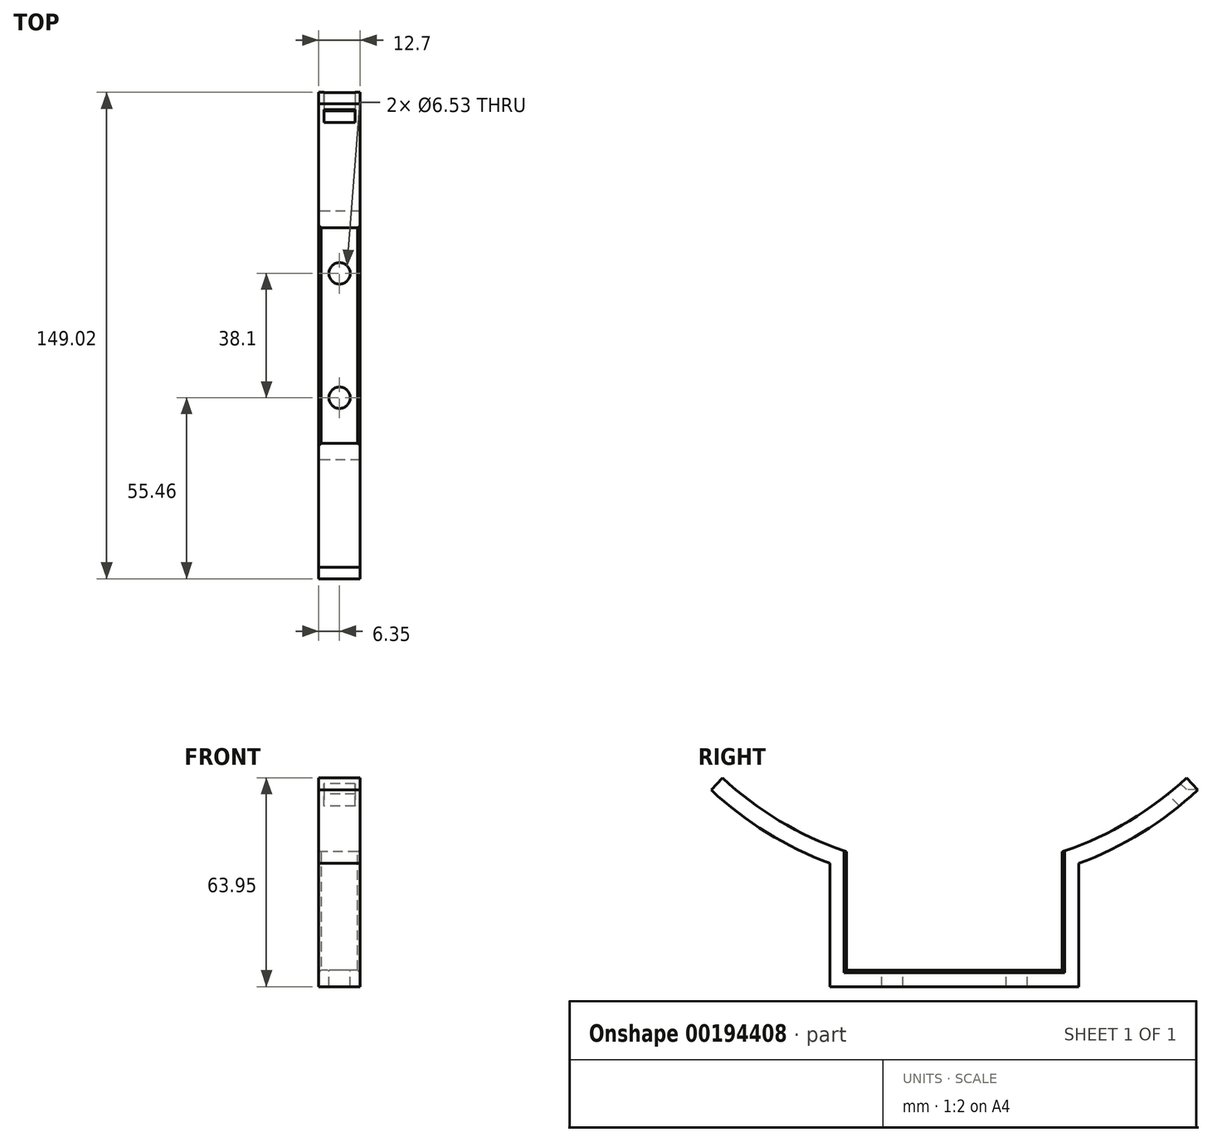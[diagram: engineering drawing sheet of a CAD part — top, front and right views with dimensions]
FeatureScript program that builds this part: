
annotation { "Feature Type Name" : "Feature", "Feature Type Description" : "" }
export const myFeature = defineFeature(function(context is Context, id is Id, definition is map)
    precondition{}
    {
        {
            var Q0;
            Q0=qCreatedBy(makeId("Right.planeOp"),FACE);
            var sketch = newSketch(context, id + "F0", { "sketchPlane" : qUnion([Q0])});
            skLineSegment(sketch, "E0", {"start": v(0, 0) * mm, "end": v(-38.1, 0) * mm});
            skLineSegment(sketch, "E1", {"start": v(-38.1, 0) * mm, "end": v(-38.1, 37.74) * mm});
            skLineSegment(sketch, "E2", {"start": v(0, 5.08) * mm, "end": v(0, 38.1) * mm});
            skLineSegment(sketch, "E3", {"start": v(0, 38.1) * mm, "end": v(0, 135.02) * mm});
            skLineSegment(sketch, "E4", {"start": v(0, 135.02) * mm, "end": v(0, 239.16) * mm});
            skLineSegment(sketch, "E5", {"start": v(0, 135.02) * mm, "end": v(0, 140.1) * mm});
            skArc(sketch, "E6", {"start": v(-71.04, 63.95) * mm, "mid": v(-53.25, 50.6) * mm, "end": v(-33.02, 41.33) * mm});
            skLineSegment(sketch, "E7.0", {"start": v(-33.02, 5.08) * mm, "end": v(-33.02, 38.1) * mm});
            skLineSegment(sketch, "E7.1", {"start": v(0, 5.08) * mm, "end": v(-33.02, 5.08) * mm});
            skArc(sketch, "E8.0", {"start": v(-74.5, 60.24) * mm, "mid": v(-57.42, 47.19) * mm, "end": v(-38.1, 37.74) * mm});
            skLineSegment(sketch, "E9", {"start": v(-71.04, 63.95) * mm, "end": v(-74.5, 60.24) * mm});
            skLineSegment(sketch, "E10", {"start": v(-33.02, 38.1) * mm, "end": v(-33.02, 41.33) * mm});
            skLineSegment(sketch, "E11.MirrorCS", {"start": v(33.02, 38.1) * mm, "end": v(33.02, 41.33) * mm});
            skLineSegment(sketch, "E12.MirrorCS", {"start": v(0, 0) * mm, "end": v(38.1, 0) * mm});
            skLineSegment(sketch, "E13.MirrorCS", {"start": v(33.02, 5.08) * mm, "end": v(33.02, 38.1) * mm});
            skArc(sketch, "E14.MirrorCS", {"start": v(71.04, 63.95) * mm, "mid": v(53.25, 50.6) * mm, "end": v(33.02, 41.33) * mm});
            skLineSegment(sketch, "E15.MirrorCS", {"start": v(0, 5.08) * mm, "end": v(33.02, 5.08) * mm});
            skLineSegment(sketch, "E16.MirrorCS", {"start": v(38.1, 0) * mm, "end": v(38.1, 37.74) * mm});
            skArc(sketch, "E17.MirrorCS", {"start": v(74.5, 60.24) * mm, "mid": v(57.42, 47.19) * mm, "end": v(38.1, 37.74) * mm});
            skLineSegment(sketch, "E18.MirrorCS", {"start": v(71.04, 63.95) * mm, "end": v(74.5, 60.24) * mm});
            skSolve(sketch);
        }
        {
            var Q0;
            Q0=makeQuery(id+"F0.imprint","IMPRINT",FACE,{"disambiguationData":[TD([[makeQuery(id+"F0.imprint","IMPRINT",EDGE,{"derivedFrom":sQuery(id+"F0.wireOp",EDGE,"E0")}),-1.0]])]});
            extrude(context, id + "F1", {"entities" : qUnion([Q0]), "depth" : 12.7 * mm});
        }
        {
            var Q0;
            Q0=makeQuery(id+"F1.opExtrude","SWEPT_FACE",FACE,{"disambiguationData":[OSD([sQuery(id+"F0.wireOp",EDGE,"E7.1"),sQuery(id+"F0.wireOp",EDGE,"E15.MirrorCS")])]});
            var sketch = newSketch(context, id + "F2", { "sketchPlane" : qUnion([Q0])});
            skLineSegment(sketch, "E19", {"start": v(0, 0) * mm, "end": v(6.35, 0) * mm});
            skLineSegment(sketch, "E20", {"start": v(6.35, 0) * mm, "end": v(6.35, 19.05) * mm});
            skLineSegment(sketch, "E21.MirrorCS", {"start": v(6.35, 0) * mm, "end": v(6.35, -19.05) * mm});
            skSolve(sketch);
        }
        {
            var Q0;
            Q0=sQuery(id+"F2.wireOp",VERTEX,"E20.end");
            var Q1;
            Q1=sQuery(id+"F2.wireOp",VERTEX,"E21.MirrorCS.end");
            var Q2;
            Q2=makeQuery(id+"F1.opExtrude","SWEPT_BODY",BODY,{"disambiguationData":[OSD([sQuery(id+"F0.wireOp",EDGE,"E0"),sQuery(id+"F0.wireOp",EDGE,"E1"),sQuery(id+"F0.wireOp",EDGE,"E6"),sQuery(id+"F0.wireOp",EDGE,"E7.0"),sQuery(id+"F0.wireOp",EDGE,"E7.1"),sQuery(id+"F0.wireOp",EDGE,"E8.0"),sQuery(id+"F0.wireOp",EDGE,"E9"),sQuery(id+"F0.wireOp",EDGE,"E10"),sQuery(id+"F0.wireOp",EDGE,"E11.MirrorCS"),sQuery(id+"F0.wireOp",EDGE,"E12.MirrorCS"),sQuery(id+"F0.wireOp",EDGE,"E13.MirrorCS"),sQuery(id+"F0.wireOp",EDGE,"E14.MirrorCS"),sQuery(id+"F0.wireOp",EDGE,"E15.MirrorCS"),sQuery(id+"F0.wireOp",EDGE,"E16.MirrorCS"),sQuery(id+"F0.wireOp",EDGE,"E17.MirrorCS"),sQuery(id+"F0.wireOp",EDGE,"E18.MirrorCS")])]});
            hole(context, id + "F3", {"style" : HoleStyle.SIMPLE, "endStyle" : HoleEndStyle.BLIND, "standardTappedOrClearance" : lookupTablePath({ "standard" : "ANSI", "fit" : "Close", "size" : "1/4", "type" : "Clearance" }), "standardBlindInLast" : lookupTablePath({ "fit" : "Close", "standard" : "ANSI", "size" : "1/4", "type" : "Clearance" }), "holeDiameter" : 6.53 * mm, "holeDepth" : 25.4 * mm, "locations" : qUnion([Q0, Q1]), "scope" : qUnion([Q2])});
        }
        {
            var Q0;
            Q0=makeQuery(id+"F1.opExtrude","SWEPT_EDGE",EDGE,{"disambiguationData":[OSD([sQuery(id+"F0.wireOp",EDGE,"E14.MirrorCS"),sQuery(id+"F0.wireOp",EDGE,"E18.MirrorCS")])]});
            cPlane(context, id + "F4", {"entities" : qUnion([Q0]), "cplaneType" : CPlaneType.LINE_ANGLE, "offset" : 25.4 * mm, "angle" : 45 * degree, "width" : 152.4 * mm, "height" : 152.4 * mm});
        }
        {
            var Q0;
            Q0=makeQuery(id+"F1.opExtrude","SWEPT_EDGE",EDGE,{"disambiguationData":[OSD([sQuery(id+"F0.wireOp",EDGE,"E6"),sQuery(id+"F0.wireOp",EDGE,"E9")])]});
            cPlane(context, id + "F5", {"entities" : qUnion([Q0]), "cplaneType" : CPlaneType.LINE_ANGLE, "offset" : 25.4 * mm, "angle" : 135 * degree, "width" : 152.4 * mm, "height" : 152.4 * mm});
        }
        {
            var Q0;
            Q0=qCreatedBy(id+"F5.planeOp",FACE);
            var sketch = newSketch(context, id + "F6", { "sketchPlane" : qUnion([Q0])});
            skLineSegment(sketch, "E22", {"start": v(12.7, -95.46) * mm, "end": v(6.35, -95.46) * mm});
            skLineSegment(sketch, "E23", {"start": v(6.35, -95.46) * mm, "end": v(6.35, -90.38) * mm});
            skLineSegment(sketch, "E24.bottom", {"start": v(11.11, -92.92) * mm, "end": v(1.59, -92.92) * mm});
            skLineSegment(sketch, "E24.top", {"start": v(11.11, -87.84) * mm, "end": v(1.59, -87.84) * mm});
            skLineSegment(sketch, "E24.left", {"start": v(11.11, -92.92) * mm, "end": v(11.11, -87.84) * mm});
            skLineSegment(sketch, "E24.right", {"start": v(1.59, -92.92) * mm, "end": v(1.59, -87.84) * mm});
            skPoint(sketch, "E24.middle", {"position": v(6.35, -90.38) * mm});
            skSolve(sketch);
        }
        {
            var Q0;
            Q0=qCreatedBy(id+"F4.planeOp",FACE);
            var sketch = newSketch(context, id + "F7", { "sketchPlane" : qUnion([Q0])});
            skLineSegment(sketch, "E25", {"start": v(12.7, 95.46) * mm, "end": v(6.35, 95.46) * mm});
            skPoint(sketch, "E26.middle", {"position": v(6.35, 100.54) * mm});
            skLineSegment(sketch, "E27.MirrorCS", {"start": v(1.59, 92.92) * mm, "end": v(1.59, 87.84) * mm});
            skLineSegment(sketch, "E28.MirrorCS", {"start": v(11.11, 92.92) * mm, "end": v(11.11, 87.84) * mm});
            skLineSegment(sketch, "E29.MirrorCS", {"start": v(11.11, 87.84) * mm, "end": v(1.59, 87.84) * mm});
            skLineSegment(sketch, "E30.MirrorCS", {"start": v(11.11, 92.92) * mm, "end": v(1.59, 92.92) * mm});
            skLineSegment(sketch, "E31.MirrorCS", {"start": v(6.35, 95.46) * mm, "end": v(6.35, 90.38) * mm});
            skPoint(sketch, "E32.MirrorP", {"position": v(6.35, 90.38) * mm});
            skPoint(sketch, "E26.right.start.orphan", {"position": v(1.59, 98) * mm});
            skPoint(sketch, "E26.top.end.orphan", {"position": v(1.59, 103.08) * mm});
            skPoint(sketch, "E26.left.end.orphan", {"position": v(11.11, 103.08) * mm});
            skPoint(sketch, "E26.bottom.start.orphan", {"position": v(11.11, 98) * mm});
            skSolve(sketch);
        }
        {
            var Q0;
            Q0=makeQuery(id+"F6.imprint","IMPRINT",FACE,{"disambiguationData":[TD([[makeQuery(id+"F6.imprint","IMPRINT",EDGE,{"derivedFrom":sQuery(id+"F6.wireOp",EDGE,"E24.top")}),1.0]])]});
            extrude(context, id + "F8", {"entities" : qUnion([Q0]), "operationType" : NewBodyOperationType.REMOVE, "endBound" : BoundingType.SYMMETRIC, "oppositeDirection" : true, "depth" : 25.4 * mm});
        }
        {
            var Q0;
            {var subQ0=sQuery(id+"F7.wireOp",EDGE,"E27.MirrorCS");Q0=makeQuery(id+"F7.imprint","IMPRINT",FACE,{"disambiguationData":[TD([[makeQuery(id+"F7.imprint","IMPRINT",EDGE,{"derivedFrom":subQ0}),1.0]])]});}
            extrude(context, id + "F9", {"entities" : qUnion([Q0]), "operationType" : NewBodyOperationType.REMOVE, "endBound" : BoundingType.SYMMETRIC, "oppositeDirection" : true, "depth" : 25.4 * mm});
        }
        {
            var Q0;
            Q0=makeQuery(id+"F9.boolean.opBoolean","INTERSECT",EDGE,{"derivedFrom":[makeQuery(id+"F1.opExtrude","SWEPT_FACE",FACE,{"disambiguationData":[OSD([sQuery(id+"F0.wireOp",EDGE,"E17.MirrorCS")])]}),makeQuery(id+"F9.opExtrude","SWEPT_FACE",FACE,{"disambiguationData":[OSD([sQuery(id+"F7.wireOp",EDGE,"E30.MirrorCS")])]})]});
            var Q1;
            Q1=makeQuery(id+"F8.boolean.opBoolean","INTERSECT",EDGE,{"derivedFrom":[makeQuery(id+"F1.opExtrude","SWEPT_FACE",FACE,{"disambiguationData":[OSD([sQuery(id+"F0.wireOp",EDGE,"E8.0")])]}),makeQuery(id+"F8.opExtrude","SWEPT_FACE",FACE,{"disambiguationData":[OSD([sQuery(id+"F6.wireOp",EDGE,"E24.bottom")])]})]});
            chamfer(context, id + "F10", {"entities" : qUnion([Q0, Q1]), "width" : 2.54 * mm, "tangentPropagation" : true});
        }
        {
            var Q0;
            Q0=makeQuery(id+"F1.opExtrude","CAP_EDGE",EDGE,{"disambiguationData":[OSD([sQuery(id+"F0.wireOp",EDGE,"E7.0"),sQuery(id+"F0.wireOp",EDGE,"E10")])],"isStart":false});
            var Q1;
            Q1=makeQuery(id+"F1.opExtrude","CAP_EDGE",EDGE,{"disambiguationData":[OSD([sQuery(id+"F0.wireOp",EDGE,"E7.1"),sQuery(id+"F0.wireOp",EDGE,"E15.MirrorCS")])],"isStart":false});
            var Q2;
            Q2=makeQuery(id+"F1.opExtrude","CAP_EDGE",EDGE,{"disambiguationData":[OSD([sQuery(id+"F0.wireOp",EDGE,"E7.1"),sQuery(id+"F0.wireOp",EDGE,"E15.MirrorCS")])],"isStart":true});
            var Q3;
            Q3=makeQuery(id+"F1.opExtrude","CAP_EDGE",EDGE,{"disambiguationData":[OSD([sQuery(id+"F0.wireOp",EDGE,"E7.0"),sQuery(id+"F0.wireOp",EDGE,"E10")])],"isStart":true});
            var Q4;
            Q4=makeQuery(id+"F1.opExtrude","CAP_EDGE",EDGE,{"disambiguationData":[OSD([sQuery(id+"F0.wireOp",EDGE,"E11.MirrorCS"),sQuery(id+"F0.wireOp",EDGE,"E13.MirrorCS")])],"isStart":true});
            var Q5;
            Q5=makeQuery(id+"F1.opExtrude","CAP_EDGE",EDGE,{"disambiguationData":[OSD([sQuery(id+"F0.wireOp",EDGE,"E11.MirrorCS"),sQuery(id+"F0.wireOp",EDGE,"E13.MirrorCS")])],"isStart":false});
            chamfer(context, id + "F11", {"entities" : qUnion([Q0, Q1, Q2, Q3, Q4, Q5]), "width" : 0.76 * mm, "tangentPropagation" : true});
        }
    });
